# Revit family: Discharge Pressure Switch-JCI_Sapphire_Plus-(70bar)Novec1230
name_source: partatom
category: Specialty Equipment
revit_build: Autodesk Revit 2017 (Build: 20171027_0315(x64)
units: mm (PartAtom-declared; Revit-internal decimal feet)

## family parameters
Always vertical = No
Cut with Voids When Loaded = No
OmniClass Number = 23.29.33.13.11
Part Type = Normal
Room Calculation Point = No
Round Connector Dimension = Use Diameter
Shared = No
Work Plane-Based = Yes

## types (1)
- Discharge Pressure Switch-JCI_Sapphire_Plus-(70bar)Novec1230
    Conduit Cutout = 6.4 mm
    Conduit Diameter 1/2" = 12.7 mm
    Conduit Diameter 3/4" = 19.1 mm
    Cover Material = JCI-Plastic-Red
    Date Modified = YYYY/MM/DD
    Default Elevation = 0.0 mm
    Depth = 67.0 mm
    Description = Manual Actuator
    Equipment Abbreviation = DPS
    Face Plate Fixing Screw = 95.0 mm
    Face Plate Fixing Screw Upper & Bottom = 105.0 mm
    Family Version = 1.0
    Fire Suppression Agent = 3M™ Novec™ 1230 Fire Protection Fluid
    Left Side Conduit Cutout = 28.0 mm
    Length = 47.6 mm
    Manufacturer = Johnson Controls, Inc.
    Model = 305.209.009
    Model Disclaimer = For More Information JOHNSON CONTROLS
    Mounting Bracket = 20.0 mm
    Mounting Bracket Offset = 5.0 mm
    Mounting Bracket Vertical Offset = 15.0 mm
    Mouting Hole Dia = 4.0 mm
    Operating Temperature = 122 °F
    Pipe Diameter = 12.7 mm
    Plunger Material = JCI-Metal-Brass-Satin
    Product Documentation Link = http://www.sapphireplus.com
    Product Material = JCI-Metal-Brass-Satin ; JCI-Plastic-Red
    Product Page URL = http://www.sapphireplus.com
    Switch Depth = 67.0 mm
    Switch Height = 114.0 mm
    Switch Width = 114.0 mm
    Thickness = 2.0 mm
    URL = https://www.ansul.com
    Washer Radius = 4.0 mm
    Weight = 2.20 lbf

## geometry (parser evidence)
native form markers: Sweep x2
no freeform markers — native parametric forms only
